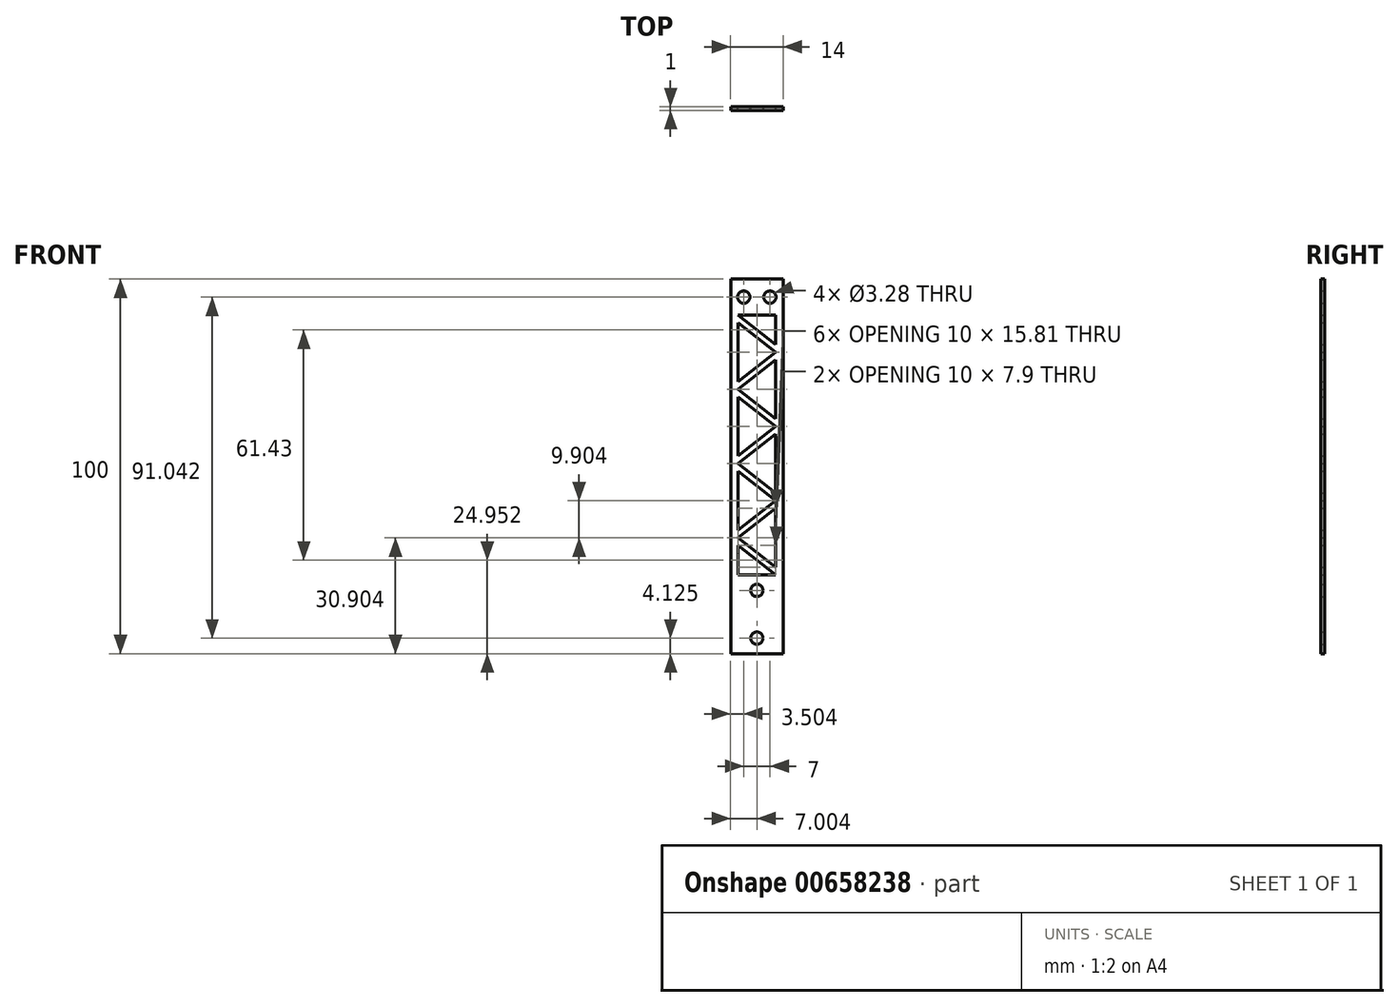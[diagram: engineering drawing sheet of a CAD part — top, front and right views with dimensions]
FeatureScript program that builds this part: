
annotation { "Feature Type Name" : "Feature", "Feature Type Description" : "" }
export const myFeature = defineFeature(function(context is Context, id is Id, definition is map)
    precondition{}
    {
        {
            var Q0;
            Q0=qCreatedBy(makeId("Front.planeOp"),FACE);
            var sketch = newSketch(context, id + "F0", { "sketchPlane" : qUnion([Q0])});
            skPoint(sketch, "E0.middle", {"position": v(-0.15, 1.7) * mm});
            skLineSegment(sketch, "E1.top", {"start": v(-7.15, -48.3) * mm, "end": v(6.85, -48.3) * mm});
            skLineSegment(sketch, "E1.right", {"start": v(6.85, 51.7) * mm, "end": v(6.85, -48.3) * mm});
            skLineSegment(sketch, "E2", {"start": v(5.85, 22.07) * mm, "end": v(5.85, 22.07) * mm});
            skLineSegment(sketch, "E3", {"start": v(-7.15, 51.7) * mm, "end": v(6.85, 51.7) * mm});
            skLineSegment(sketch, "E4", {"start": v(-7.15, -48.3) * mm, "end": v(-7.15, 51.7) * mm});
            skLineSegment(sketch, "E5", {"start": v(4.85, -27.3) * mm, "end": v(-5.15, -27.3) * mm});
            skLineSegment(sketch, "E6", {"start": v(4.85, 42.02) * mm, "end": v(-5.15, 42.02) * mm});
            skCircle(sketch, "E7", {"center": v(3.35, 46.86) * mm, "radius": 1.64 * mm});
            skCircle(sketch, "E8.MirrorC", {"center": v(-3.65, 46.86) * mm, "radius": 1.64 * mm});
            skCircle(sketch, "E9", {"center": v(-0.15, -31.43) * mm, "radius": 1.64 * mm});
            skCircle(sketch, "E10.MirrorC", {"center": v(-0.15, -44.18) * mm, "radius": 1.64 * mm});
            skLineSegment(sketch, "E11", {"start": v(4.85, 34.12) * mm, "end": v(-5.15, 42.02) * mm});
            skLineSegment(sketch, "E12", {"start": v(-5.15, 24.21) * mm, "end": v(-5.15, 40.02) * mm});
            skLineSegment(sketch, "E13", {"start": v(-5.15, 40.02) * mm, "end": v(4.85, 32.12) * mm});
            skLineSegment(sketch, "E14", {"start": v(4.85, 34.12) * mm, "end": v(4.85, 42.02) * mm});
            skLineSegment(sketch, "E15", {"start": v(-5.15, 24.21) * mm, "end": v(4.85, 32.12) * mm});
            skLineSegment(sketch, "E16", {"start": v(4.85, 30.12) * mm, "end": v(-5.15, 22.21) * mm});
            skLineSegment(sketch, "E17", {"start": v(-5.15, 22.21) * mm, "end": v(4.85, 14.31) * mm});
            skLineSegment(sketch, "E18", {"start": v(4.85, 12.3) * mm, "end": v(-5.15, 20.21) * mm});
            skLineSegment(sketch, "E19", {"start": v(-5.15, 20.21) * mm, "end": v(-5.15, 4.4) * mm});
            skLineSegment(sketch, "E20", {"start": v(-5.15, 4.4) * mm, "end": v(4.85, 12.3) * mm});
            skLineSegment(sketch, "E21", {"start": v(4.85, 30.12) * mm, "end": v(4.85, 14.31) * mm});
            skLineSegment(sketch, "E22", {"start": v(-5.15, 2.4) * mm, "end": v(4.85, 10.3) * mm});
            skLineSegment(sketch, "E23", {"start": v(-5.15, 2.4) * mm, "end": v(4.85, -5.5) * mm});
            skLineSegment(sketch, "E24", {"start": v(-5.15, 0.4) * mm, "end": v(4.85, -7.5) * mm});
            skLineSegment(sketch, "E25", {"start": v(-5.15, -15.4) * mm, "end": v(4.85, -7.5) * mm});
            skLineSegment(sketch, "E26", {"start": v(4.85, -9.5) * mm, "end": v(-5.15, -17.4) * mm});
            skLineSegment(sketch, "E27", {"start": v(4.85, -25.3) * mm, "end": v(-5.15, -17.4) * mm});
            skLineSegment(sketch, "E28", {"start": v(-5.15, -27.3) * mm, "end": v(-5.15, -19.4) * mm});
            skLineSegment(sketch, "E29", {"start": v(-5.15, -19.4) * mm, "end": v(4.85, -27.3) * mm});
            skLineSegment(sketch, "E30", {"start": v(4.85, 10.3) * mm, "end": v(4.85, -5.5) * mm});
            skLineSegment(sketch, "E31", {"start": v(-5.15, 0.4) * mm, "end": v(-5.15, -15.4) * mm});
            skLineSegment(sketch, "E32", {"start": v(4.85, -9.5) * mm, "end": v(4.85, -25.3) * mm});
            skSolve(sketch);
        }
        {
            var Q0;
            Q0 = qSketchRegion(id + "F0", true);
            extrude(context, id + "F1", {"entities" : qUnion([Q0]), "depth" : 1 * mm, "offsetDistance" : 25 * mm});
        }
    });
